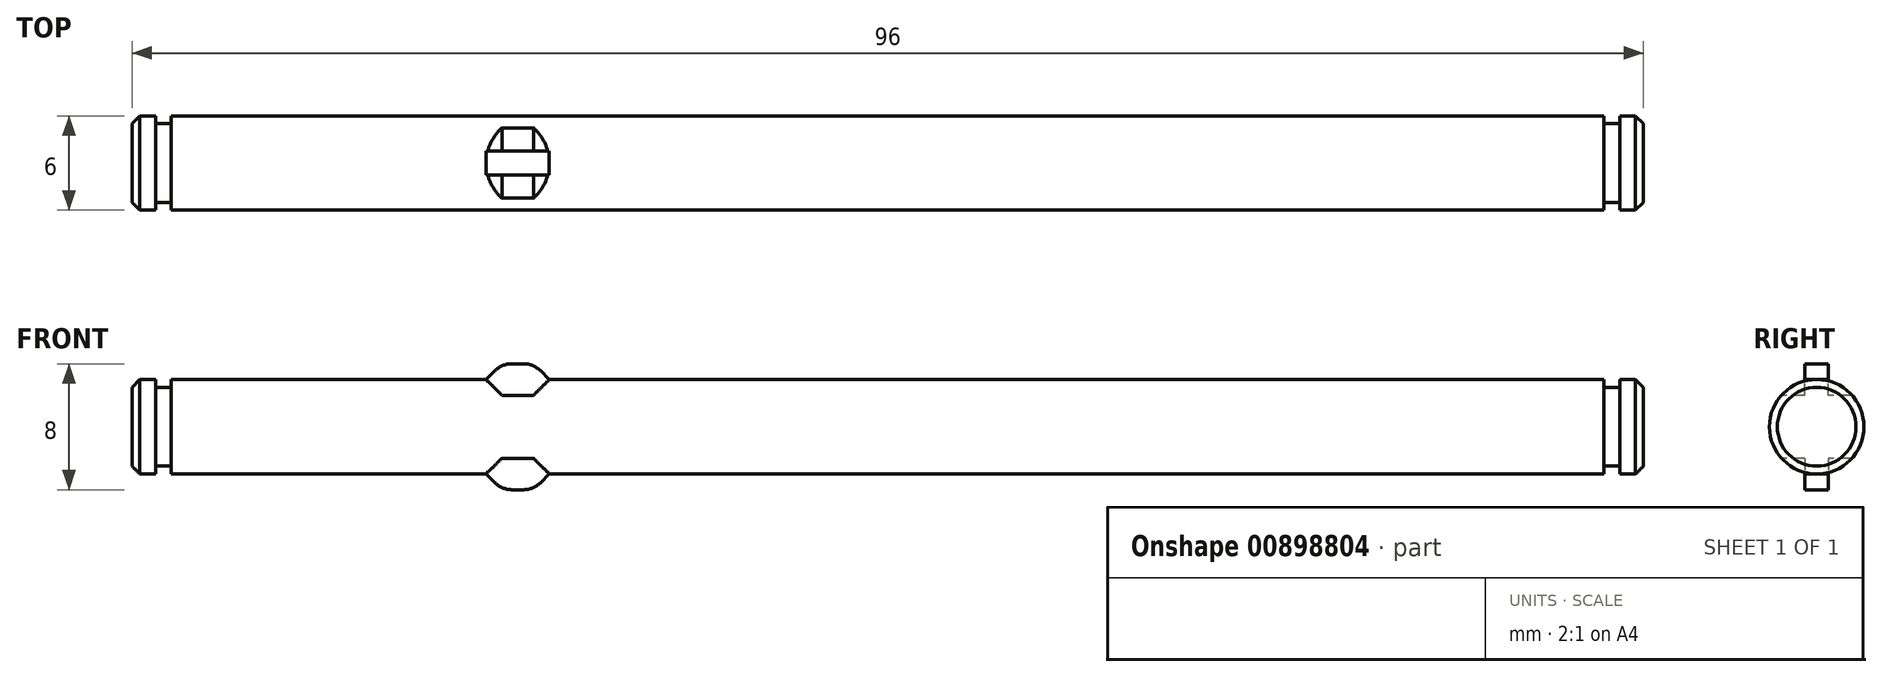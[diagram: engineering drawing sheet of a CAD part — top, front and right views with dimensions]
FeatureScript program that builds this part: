
annotation { "Feature Type Name" : "Feature", "Feature Type Description" : "" }
export const myFeature = defineFeature(function(context is Context, id is Id, definition is map)
    precondition{}
    {
        {
            var Q0;
            Q0=qCreatedBy(makeId("Right.planeOp"),FACE);
            var sketch = newSketch(context, id + "F0", { "sketchPlane" : qUnion([Q0])});
            skCircle(sketch, "E0", {"center": v(0, 0) * mm, "radius": 3 * mm});
            skSolve(sketch);
        }
        {
            var Q0;
            Q0 = qSketchRegion(id + "F0", true);
            extrude(context, id + "F1", {"entities" : qUnion([Q0]), "depth" : 96 * mm, "offsetDistance" : 25 * mm});
        }
        {
            var Q0;
            Q0=makeQuery(id+"F1.opExtrude","CAP_EDGE",EDGE,{"disambiguationData":[OSD([sQuery(id+"F0.wireOp",EDGE,"E0")])],"isStart":true});
            var Q1;
            Q1=makeQuery(id+"F1.opExtrude","CAP_EDGE",EDGE,{"disambiguationData":[OSD([sQuery(id+"F0.wireOp",EDGE,"E0")])],"isStart":false});
            chamfer(context, id + "F2", {"entities" : qUnion([Q0, Q1]), "width" : .5 * mm, "tangentPropagation" : true});
        }
        {
            var Q0;
            Q0=qCreatedBy(makeId("Front.planeOp"),FACE);
            var sketch = newSketch(context, id + "F3", { "sketchPlane" : qUnion([Q0])});
            skLineSegment(sketch, "E1.bottom", {"start": v(1.5, 3.5) * mm, "end": v(2.5, 3.5) * mm});
            skLineSegment(sketch, "E1.top", {"start": v(1.5, 2.5) * mm, "end": v(2.5, 2.5) * mm});
            skLineSegment(sketch, "E1.left", {"start": v(1.5, 3.5) * mm, "end": v(1.5, 2.5) * mm});
            skLineSegment(sketch, "E1.right", {"start": v(2.5, 3.5) * mm, "end": v(2.5, 2.5) * mm});
            skLineSegment(sketch, "E2", {"start": v(48, 7.9) * mm, "end": v(48, -11.23) * mm});
            skLineSegment(sketch, "E3.MirrorCS", {"start": v(93.5, 3.5) * mm, "end": v(93.5, 2.5) * mm});
            skLineSegment(sketch, "E4.MirrorCS", {"start": v(94.5, 3.5) * mm, "end": v(93.5, 3.5) * mm});
            skLineSegment(sketch, "E5.MirrorCS", {"start": v(94.5, 3.5) * mm, "end": v(94.5, 2.5) * mm});
            skLineSegment(sketch, "E6.MirrorCS", {"start": v(94.5, 2.5) * mm, "end": v(93.5, 2.5) * mm});
            skLineSegment(sketch, "E7", {"start": v(37.38, 0) * mm, "end": v(58.92, 0) * mm});
            skSolve(sketch);
        }
        {
            var Q0;
            Q0 = qSketchRegion(id + "F3", true);
            var Q1;
            Q1=sQuery(id+"F3.wireOp",EDGE,"E7");
            revolve(context, id + "F4", {"operationType" : NewBodyOperationType.REMOVE, "surfaceOperationType" : NewSurfaceOperationType.NEW, "entities" : qUnion([Q0]), "axis" : qUnion([Q1]), "revolveType" : RevolveType.FULL, "oppositeDirection" : true});
        }
        {
            var Q0;
            Q0=qCreatedBy(makeId("Front.planeOp"),FACE);
            var sketch = newSketch(context, id + "F5", { "sketchPlane" : qUnion([Q0])});
            skLineSegment(sketch, "E8.bottom", {"start": v(22.5, 4) * mm, "end": v(26.5, 4) * mm});
            skLineSegment(sketch, "E8.top", {"start": v(23.5, 2) * mm, "end": v(25.5, 2) * mm});
            skLineSegment(sketch, "E8.left", {"start": v(22.5, 4) * mm, "end": v(22.5, 3) * mm});
            skLineSegment(sketch, "E8.right", {"start": v(26.5, 4) * mm, "end": v(26.5, 3) * mm});
            skLineSegment(sketch, "E9", {"start": v(22.5, 3) * mm, "end": v(23.5, 2) * mm});
            skLineSegment(sketch, "E10", {"start": v(26.5, 3) * mm, "end": v(25.5, 2) * mm});
            skPoint(sketch, "E11.orphan", {"position": v(22.5, 2) * mm});
            skPoint(sketch, "E12.orphan", {"position": v(26.5, 2) * mm});
            skLineSegment(sketch, "E13", {"start": v(0, 0) * mm, "end": v(29.92, 0) * mm});
            skLineSegment(sketch, "E14.MirrorCS", {"start": v(26.5, -3) * mm, "end": v(25.5, -2) * mm});
            skLineSegment(sketch, "E15.MirrorCS", {"start": v(22.5, -3) * mm, "end": v(23.5, -2) * mm});
            skLineSegment(sketch, "E16.MirrorCS", {"start": v(22.5, -4) * mm, "end": v(22.5, -3) * mm});
            skPoint(sketch, "E17.MirrorP", {"position": v(22.5, -2) * mm});
            skLineSegment(sketch, "E18.MirrorCS", {"start": v(26.5, -4) * mm, "end": v(26.5, -3) * mm});
            skLineSegment(sketch, "E19.MirrorCS", {"start": v(22.5, -4) * mm, "end": v(26.5, -4) * mm});
            skLineSegment(sketch, "E20.MirrorCS", {"start": v(23.5, -2) * mm, "end": v(25.5, -2) * mm});
            skPoint(sketch, "E21.MirrorP", {"position": v(26.5, -2) * mm});
            skSolve(sketch);
        }
        {
            var Q0;
            Q0 = qSketchRegion(id + "F5", true);
            extrude(context, id + "F6", {"entities" : qUnion([Q0]), "operationType" : NewBodyOperationType.REMOVE, "endBound" : BoundingType.THROUGH_ALL, "oppositeDirection" : true, "depth" : 25 * mm, "offsetDistance" : 25 * mm, "hasSecondDirection" : true, "secondDirectionOppositeDirection" : false, "secondDirectionDepth" : 25 * mm});
        }
        {
            var Q0;
            Q0=qCreatedBy(makeId("Front.planeOp"),FACE);
            var sketch = newSketch(context, id + "F7", { "sketchPlane" : qUnion([Q0])});
            skLineSegment(sketch, "E22.bottom", {"start": v(22.5, 2) * mm, "end": v(26.5, 2) * mm});
            skLineSegment(sketch, "E22.top", {"start": v(23.5, 4) * mm, "end": v(25.5, 4) * mm});
            skLineSegment(sketch, "E22.left", {"start": v(22.5, 2) * mm, "end": v(22.5, 3) * mm});
            skLineSegment(sketch, "E22.right", {"start": v(26.5, 2) * mm, "end": v(26.5, 3) * mm});
            skLineSegment(sketch, "E23", {"start": v(22.5, 3) * mm, "end": v(23.5, 4) * mm});
            skLineSegment(sketch, "E24", {"start": v(26.5, 3) * mm, "end": v(25.5, 4) * mm});
            skPoint(sketch, "E25.orphan", {"position": v(22.5, 4) * mm});
            skPoint(sketch, "E26.orphan", {"position": v(26.5, 4) * mm});
            skLineSegment(sketch, "E27", {"start": v(0, 0) * mm, "end": v(35.1, 0) * mm});
            skPoint(sketch, "E28.MirrorP", {"position": v(22.5, -4) * mm});
            skLineSegment(sketch, "E29.MirrorCS", {"start": v(22.5, -3) * mm, "end": v(23.5, -4) * mm});
            skPoint(sketch, "E30.MirrorP", {"position": v(26.5, -4) * mm});
            skLineSegment(sketch, "E31.MirrorCS", {"start": v(26.5, -3) * mm, "end": v(25.5, -4) * mm});
            skLineSegment(sketch, "E32.MirrorCS", {"start": v(22.5, -2) * mm, "end": v(22.5, -3) * mm});
            skLineSegment(sketch, "E33.MirrorCS", {"start": v(26.5, -2) * mm, "end": v(26.5, -3) * mm});
            skLineSegment(sketch, "E34.MirrorCS", {"start": v(23.5, -4) * mm, "end": v(25.5, -4) * mm});
            skLineSegment(sketch, "E35.MirrorCS", {"start": v(22.5, -2) * mm, "end": v(26.5, -2) * mm});
            skSolve(sketch);
        }
        {
            var Q0;
            Q0 = qSketchRegion(id + "F7", true);
            extrude(context, id + "F8", {"entities" : qUnion([Q0]), "operationType" : NewBodyOperationType.ADD, "depth" : .75 * mm, "offsetDistance" : 25 * mm, "hasSecondDirection" : true, "secondDirectionOppositeDirection" : true, "secondDirectionDepth" : .75 * mm});
        }
        {
            var Q0;
            Q0=makeQuery(id+"F8.opExtrude","SWEPT_EDGE",EDGE,{"disambiguationData":[OSD([sQuery(id+"F7.wireOp",EDGE,"E29.MirrorCS"),sQuery(id+"F7.wireOp",EDGE,"E34.MirrorCS")])]});
            var Q1;
            Q1=makeQuery(id+"F8.opExtrude","SWEPT_EDGE",EDGE,{"disambiguationData":[OSD([sQuery(id+"F7.wireOp",EDGE,"E31.MirrorCS"),sQuery(id+"F7.wireOp",EDGE,"E34.MirrorCS")])]});
            var Q2;
            Q2=makeQuery(id+"F8.opExtrude","SWEPT_EDGE",EDGE,{"disambiguationData":[OSD([sQuery(id+"F7.wireOp",EDGE,"E22.top"),sQuery(id+"F7.wireOp",EDGE,"E23")])]});
            var Q3;
            Q3=makeQuery(id+"F8.opExtrude","SWEPT_EDGE",EDGE,{"disambiguationData":[OSD([sQuery(id+"F7.wireOp",EDGE,"E22.top"),sQuery(id+"F7.wireOp",EDGE,"E24")])]});
            fillet(context, id + "F9", {"entities" : qUnion([Q0, Q1, Q2, Q3]), "radius" : 1.5 * mm, "tangentPropagation" : true, "allowEdgeOverflow" : false});
        }
    });
